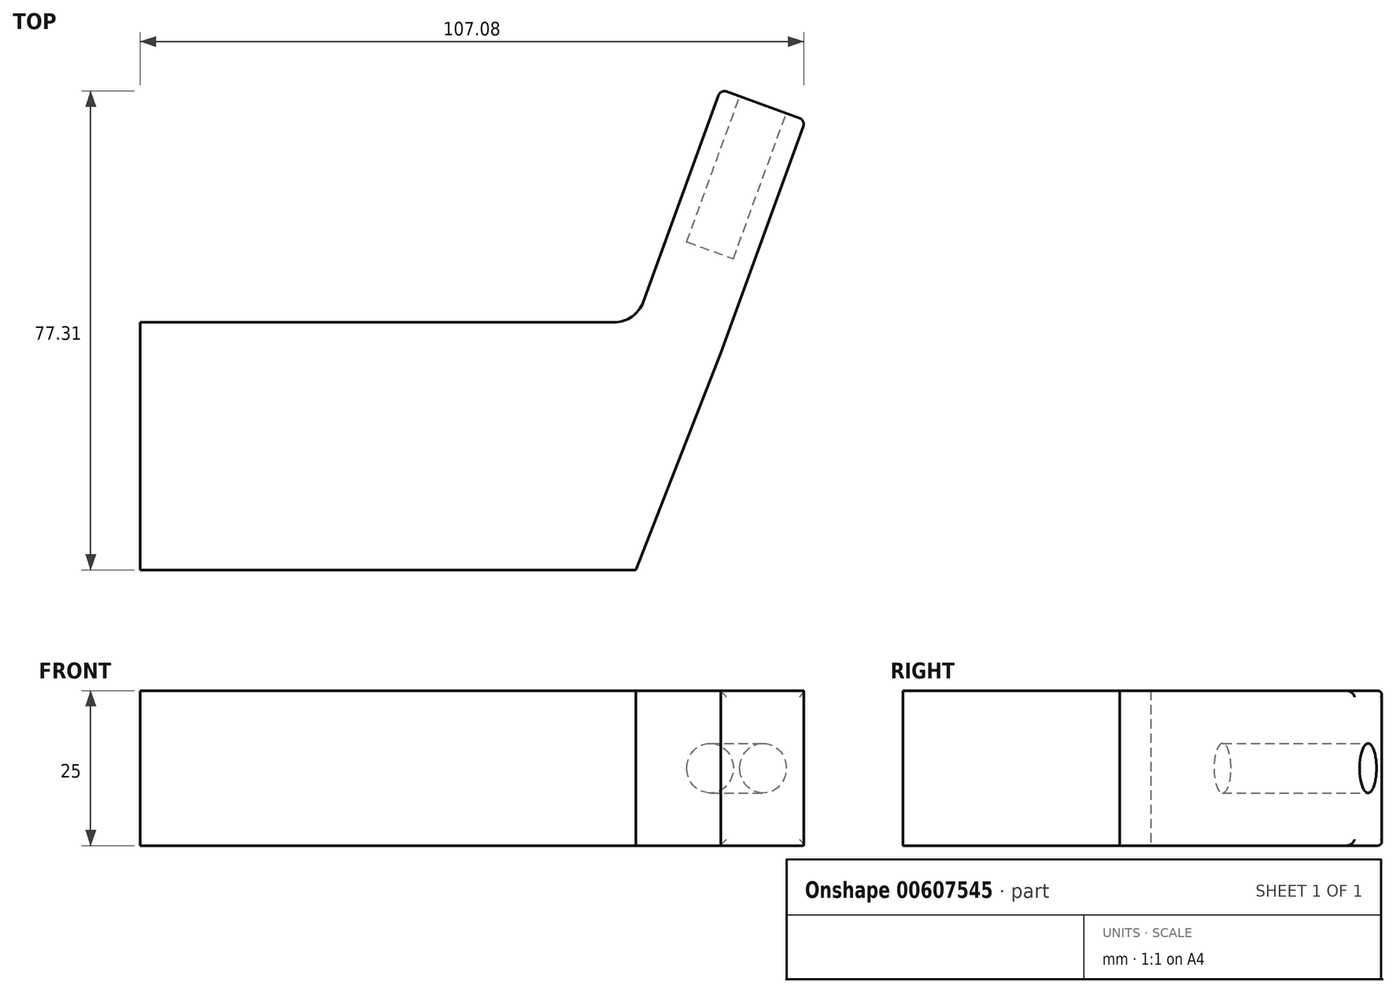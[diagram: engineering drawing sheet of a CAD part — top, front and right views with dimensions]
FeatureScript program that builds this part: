
annotation { "Feature Type Name" : "Feature", "Feature Type Description" : "" }
export const myFeature = defineFeature(function(context is Context, id is Id, definition is map)
    precondition{}
    {
        {
            var Q0;
            Q0=qCreatedBy(makeId("Top.planeOp"),FACE);
            var sketch = newSketch(context, id + "F0", { "sketchPlane" : qUnion([Q0])});
            skLineSegment(sketch, "E0.bottom", {"start": v(40.18, -16.77) * mm, "end": v(-39.82, -16.77) * mm});
            skLineSegment(sketch, "E0.top", {"start": v(40.18, 23.23) * mm, "end": v(-39.82, 23.23) * mm});
            skLineSegment(sketch, "E0.left", {"start": v(40.18, -16.77) * mm, "end": v(40.18, 23.23) * mm});
            skLineSegment(sketch, "E0.right", {"start": v(-39.82, -16.77) * mm, "end": v(-39.82, 23.23) * mm});
            skLineSegment(sketch, "E1", {"start": v(40.18, 23.23) * mm, "end": v(53.86, 60.82) * mm});
            skLineSegment(sketch, "E2", {"start": v(53.86, 18.25) * mm, "end": v(67.54, 55.84) * mm});
            skLineSegment(sketch, "E3", {"start": v(67.54, 55.84) * mm, "end": v(53.86, 60.82) * mm});
            skLineSegment(sketch, "E4", {"start": v(53.86, 18.25) * mm, "end": v(40.18, 23.23) * mm});
            skLineSegment(sketch, "E5", {"start": v(40.18, -16.77) * mm, "end": v(53.86, 18.25) * mm});
            skSolve(sketch);
        }
        {
            var Q0;
            Q0=makeQuery(id+"F0.imprint","IMPRINT",FACE,{"disambiguationData":[TD([[makeQuery(id+"F0.imprint","IMPRINT",EDGE,{"derivedFrom":sQuery(id+"F0.wireOp",EDGE,"E0.bottom")}),-1.0]])]});
            var Q1;
            Q1=makeQuery(id+"F0.imprint","IMPRINT",FACE,{"disambiguationData":[TD([[makeQuery(id+"F0.imprint","IMPRINT",EDGE,{"derivedFrom":sQuery(id+"F0.wireOp",EDGE,"E0.left")}),-1.0]])]});
            var Q2;
            Q2=makeQuery(id+"F0.imprint","IMPRINT",FACE,{"disambiguationData":[TD([[makeQuery(id+"F0.imprint","IMPRINT",EDGE,{"derivedFrom":sQuery(id+"F0.wireOp",EDGE,"E1")}),-1.0]])]});
            extrude(context, id + "F1", {"entities" : qUnion([Q0, Q1, Q2]), "depth" : 25 * mm, "offsetDistance" : 25 * mm});
        }
        {
            var Q0;
            Q0=makeQuery(id+"F1.opExtrude","SWEPT_FACE",FACE,{"disambiguationData":[OSD([sQuery(id+"F0.wireOp",EDGE,"E3")])]});
            var sketch = newSketch(context, id + "F2", { "sketchPlane" : qUnion([Q0])});
            skCircle(sketch, "E6", {"center": v(-37.09, 12.5) * mm, "radius": 4 * mm});
            skLineSegment(sketch, "E7", {"start": v(-37.09, 25) * mm, "end": v(-37.09, 0) * mm, "construction": true});
            skLineSegment(sketch, "E8", {"start": v(-29.8, 12.5) * mm, "end": v(-44.37, 12.5) * mm, "construction": true});
            skSolve(sketch);
        }
        {
            var Q0;
            Q0 = qSketchRegion(id + "F2", true);
            var Q1;
            Q1=makeQuery(id+"F2.imprint","IMPRINT",FACE,{"disambiguationData":[TD([[makeQuery(id+"F2.imprint","IMPRINT",EDGE,{"derivedFrom":sQuery(id+"F2.wireOp",EDGE,"E6")}),1.0]])]});
            extrude(context, id + "F3", {"entities" : qUnion([Q0, Q1]), "operationType" : NewBodyOperationType.REMOVE, "oppositeDirection" : true, "depth" : 25 * mm, "offsetDistance" : 25 * mm});
        }
        {
            var Q0;
            Q0=makeQuery(id+"F1.opExtrude","SWEPT_EDGE",EDGE,{"disambiguationData":[OSD([sQuery(id+"F0.wireOp",EDGE,"E0.top"),sQuery(id+"F0.wireOp",EDGE,"E0.left"),sQuery(id+"F0.wireOp",EDGE,"E1"),sQuery(id+"F0.wireOp",EDGE,"E4")])]});
            fillet(context, id + "F4", {"entities" : qUnion([Q0]), "radius" : 5 * mm, "tangentPropagation" : true, "allowEdgeOverflow" : false});
        }
        {
            var Q0;
            Q0=makeQuery(id+"F1.opExtrude","SWEPT_EDGE",EDGE,{"disambiguationData":[OSD([sQuery(id+"F0.wireOp",EDGE,"E2"),sQuery(id+"F0.wireOp",EDGE,"E3"),sQuery(id+"F0.wireOp",EDGE,"78Pym8jD-f2kb-0Bhi-7Kbv-Rxe9GSIBOdCh")])]});
            var Q1;
            Q1=makeQuery(id+"F1.opExtrude","CAP_EDGE",EDGE,{"disambiguationData":[OSD([sQuery(id+"F0.wireOp",EDGE,"E3")])],"isStart":true});
            var Q2;
            Q2=makeQuery(id+"F1.opExtrude","SWEPT_EDGE",EDGE,{"disambiguationData":[OSD([sQuery(id+"F0.wireOp",EDGE,"E1"),sQuery(id+"F0.wireOp",EDGE,"E3")])]});
            var Q3;
            Q3=makeQuery(id+"F1.opExtrude","CAP_EDGE",EDGE,{"disambiguationData":[OSD([sQuery(id+"F0.wireOp",EDGE,"E3")])],"isStart":false});
            fillet(context, id + "F5", {"entities" : qUnion([Q0, Q1, Q2, Q3]), "radius" : 1 * mm, "tangentPropagation" : true, "allowEdgeOverflow" : false});
        }
    });
